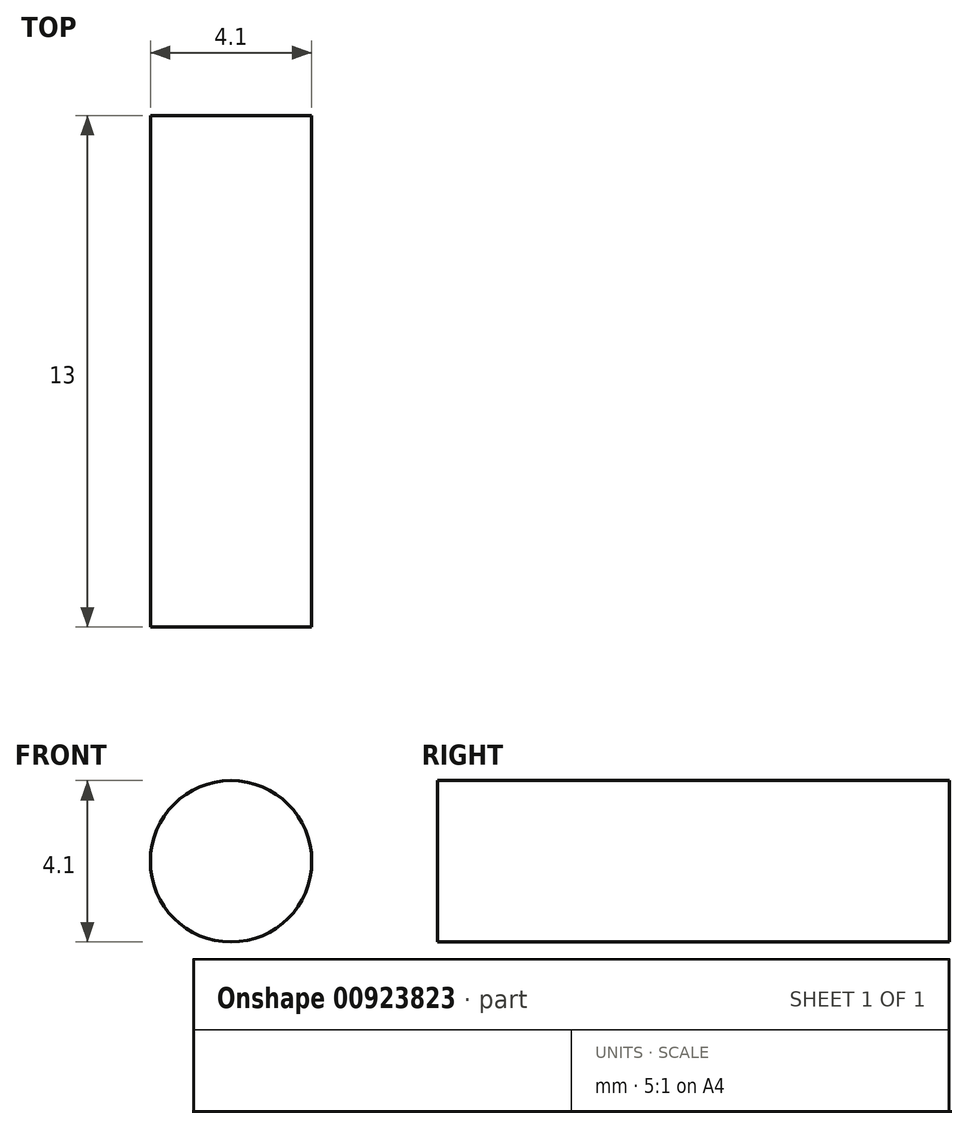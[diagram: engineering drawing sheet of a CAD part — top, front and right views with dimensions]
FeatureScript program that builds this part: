
annotation { "Feature Type Name" : "Feature", "Feature Type Description" : "" }
export const myFeature = defineFeature(function(context is Context, id is Id, definition is map)
    precondition{}
    {
        {
            var Q0;
            Q0=qCreatedBy(makeId("Front.planeOp"),FACE);
            var sketch = newSketch(context, id + "F0", { "sketchPlane" : qUnion([Q0])});
            skCircle(sketch, "E0", {"center": v(0, 0) * mm, "radius": 2.05 * mm});
            skSolve(sketch);
        }
        {
            var Q0;
            Q0=makeQuery(id+"F0.imprint","IMPRINT",FACE,{"disambiguationData":[TD([[makeQuery(id+"F0.imprint","IMPRINT",EDGE,{"derivedFrom":sQuery(id+"F0.wireOp",EDGE,"E0")}),1.0]])]});
            extrude(context, id + "F1", {"entities" : qUnion([Q0]), "depth" : 13 * mm, "offsetDistance" : 25 * mm});
        }
    });
